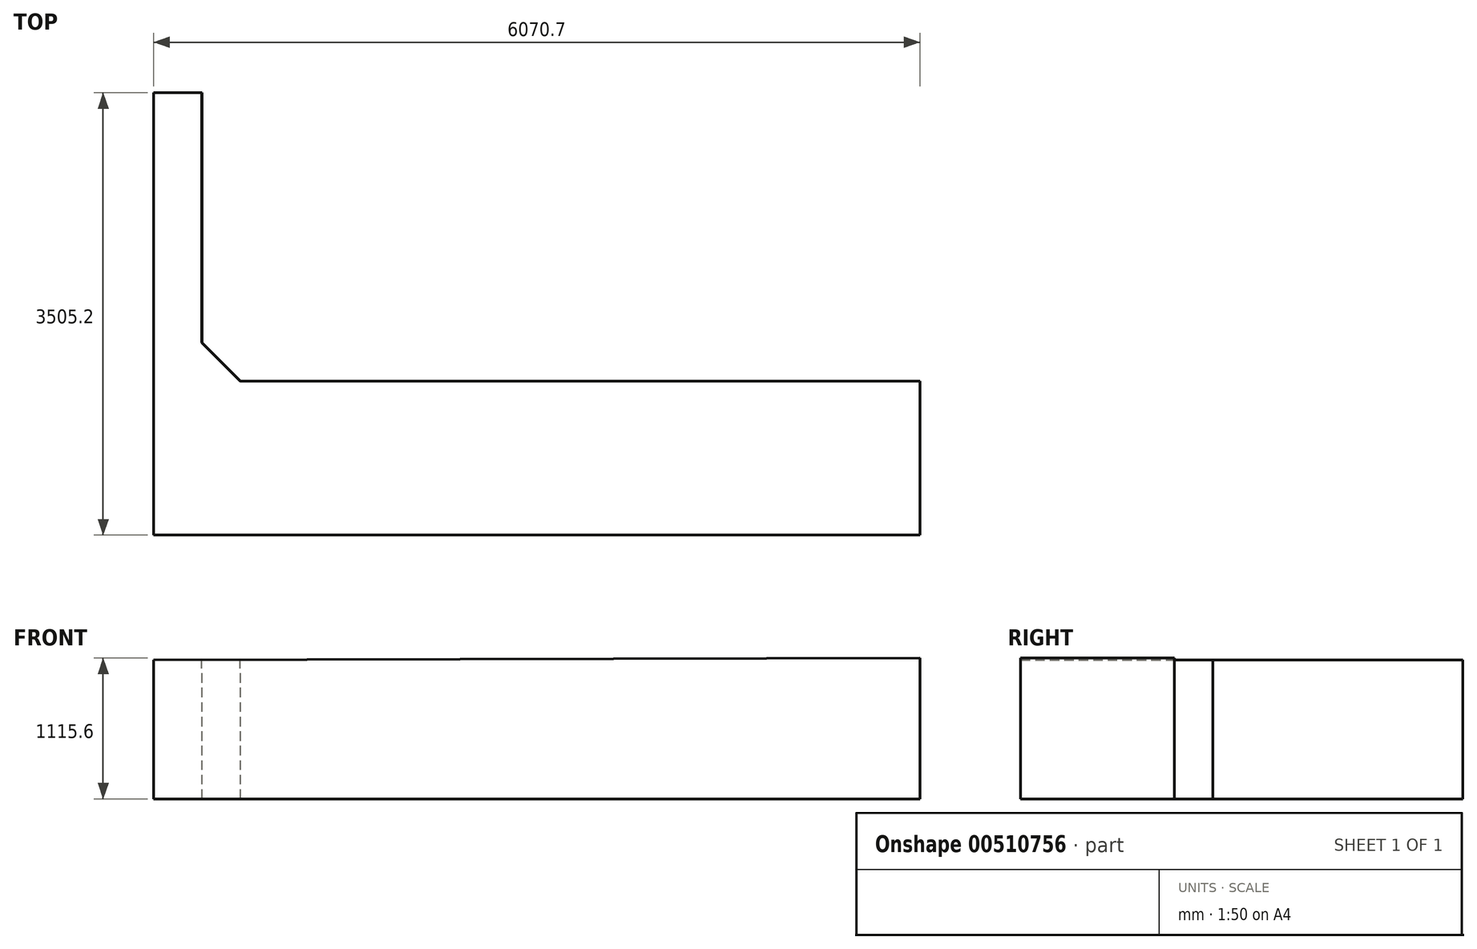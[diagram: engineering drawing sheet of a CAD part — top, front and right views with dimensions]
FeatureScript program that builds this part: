
annotation { "Feature Type Name" : "Feature", "Feature Type Description" : "" }
export const myFeature = defineFeature(function(context is Context, id is Id, definition is map)
    precondition{}
    {
        {
            var Q0;
            Q0=qCreatedBy(makeId("Right.planeOp"),FACE);
            var sketch = newSketch(context, id + "F0", { "sketchPlane" : qUnion([Q0])});
            skLineSegment(sketch, "E0.bottom", {"start": v(0, 167.64) * mm, "end": v(3505.2, 167.64) * mm});
            skLineSegment(sketch, "E0.top", {"start": v(0, 1298.45) * mm, "end": v(3505.2, 1298.45) * mm});
            skLineSegment(sketch, "E0.left", {"start": v(0, 167.64) * mm, "end": v(0, 1298.45) * mm});
            skLineSegment(sketch, "E0.right", {"start": v(3505.2, 167.64) * mm, "end": v(3505.2, 1298.45) * mm});
            skSolve(sketch);
        }
        {
            var Q0;
            Q0=qCreatedBy(makeId("Right.planeOp"),FACE);
            cPlane(context, id + "F1", {"entities" : qUnion([Q0]), "cplaneType" : CPlaneType.OFFSET, "offset" : 12115.8 * mm, "oppositeDirection" : true, "width" : 152.4 * mm, "height" : 152.4 * mm});
        }
        {
            var Q0;
            Q0=qCreatedBy(id+"F1.planeOp",FACE);
            var sketch = newSketch(context, id + "F2", { "sketchPlane" : qUnion([Q0])});
            skLineSegment(sketch, "E1.bottom", {"start": v(0, 167.64) * mm, "end": v(3505.2, 167.64) * mm});
            skLineSegment(sketch, "E1.top", {"start": v(0, 1267.97) * mm, "end": v(3505.2, 1267.97) * mm});
            skLineSegment(sketch, "E1.left", {"start": v(0, 167.64) * mm, "end": v(0, 1267.97) * mm});
            skLineSegment(sketch, "E1.right", {"start": v(3505.2, 167.64) * mm, "end": v(3505.2, 1267.97) * mm});
            skSolve(sketch);
        }
        {
            var Q0;
            Q0=makeQuery(id+"F2.imprint","IMPRINT",FACE,{"disambiguationData":[TD([[makeQuery(id+"F2.imprint","IMPRINT",EDGE,{"derivedFrom":sQuery(id+"F2.wireOp",EDGE,"E1.bottom")}),1.0]])]});
            var Q1;
            Q1=makeQuery(id+"F0.imprint","IMPRINT",FACE,{"disambiguationData":[TD([[makeQuery(id+"F0.imprint","IMPRINT",EDGE,{"derivedFrom":sQuery(id+"F0.wireOp",EDGE,"E0.bottom")}),1.0]])]});
            loft(context, id + "F3", {"sheetProfilesArray" : [{ "sheetProfileEntities" : qUnion([Q0]) }, { "sheetProfileEntities" : qUnion([Q1]) }]});
        }
        {
            var Q0;
            Q0=makeQuery(id+"F3.opLoft","SWEPT_FACE",FACE,{"disambiguationData":[OSD([sQuery(id+"F0.wireOp",EDGE,"E0.top"),sQuery(id+"F0.wireOp",EDGE,"E0.left"),sQuery(id+"F0.wireOp",EDGE,"E0.right"),sQuery(id+"F2.wireOp",EDGE,"E1.top"),sQuery(id+"F2.wireOp",EDGE,"E1.left"),sQuery(id+"F2.wireOp",EDGE,"E1.right")])]});
            var sketch = newSketch(context, id + "F4", { "sketchPlane" : qUnion([Q0])});
            skLineSegment(sketch, "E2", {"start": v(-11731.57, 3505.2) * mm, "end": v(-11731.57, 1524) * mm});
            skLineSegment(sketch, "E3", {"start": v(-11731.57, 1524) * mm, "end": v(-11426.77, 1219.2) * mm});
            skLineSegment(sketch, "E4", {"start": v(-11426.77, 1219.2) * mm, "end": v(-682.53, 1219.2) * mm});
            skLineSegment(sketch, "E5", {"start": v(-682.53, 1219.2) * mm, "end": v(-377.73, 1524) * mm});
            skLineSegment(sketch, "E6", {"start": v(-377.73, 1524) * mm, "end": v(-377.73, 3505.2) * mm});
            skLineSegment(sketch, "E7", {"start": v(-377.73, 3505.2) * mm, "end": v(-11731.57, 3505.2) * mm});
            skSolve(sketch);
        }
        {
            var Q0;
            Q0=qSketchRegion(id+"F4",true);
            extrude(context, id + "F5", {"entities" : qUnion([Q0]), "operationType" : NewBodyOperationType.REMOVE, "endBound" : BoundingType.UP_TO_NEXT, "oppositeDirection" : true, "depth" : 30.48 * mm});
        }
        {
            var Q0;
            Q0=qCreatedBy(makeId("Right.planeOp"),FACE);
            cPlane(context, id + "F6", {"entities" : qUnion([Q0]), "cplaneType" : CPlaneType.OFFSET, "offset" : 6045.1 * mm, "oppositeDirection" : true, "width" : 152.4 * mm, "height" : 152.4 * mm});
        }
        {
            var Q0;
            Q0=qCreatedBy(id+"F6.planeOp",FACE);
            var sketch = newSketch(context, id + "F7", { "sketchPlane" : qUnion([Q0])});
            skLineSegment(sketch, "E8.bottom", {"start": v(0, 0) * mm, "end": v(3505.2, 0) * mm});
            skLineSegment(sketch, "E8.top", {"start": v(0, 1371.6) * mm, "end": v(3505.2, 1371.6) * mm});
            skLineSegment(sketch, "E8.left", {"start": v(0, 0) * mm, "end": v(0, 1371.6) * mm});
            skLineSegment(sketch, "E8.right", {"start": v(3505.2, 0) * mm, "end": v(3505.2, 1371.6) * mm});
            skSolve(sketch);
        }
        {
            var Q0;
            Q0=makeQuery(id+"F7.imprint","IMPRINT",FACE,{"disambiguationData":[TD([[makeQuery(id+"F7.imprint","IMPRINT",EDGE,{"derivedFrom":sQuery(id+"F7.wireOp",EDGE,"E8.bottom")}),1.0]])]});
            extrude(context, id + "F8", {"entities" : qUnion([Q0]), "operationType" : NewBodyOperationType.REMOVE, "endBound" : BoundingType.UP_TO_NEXT, "depth" : 30.48 * mm});
        }
    });
